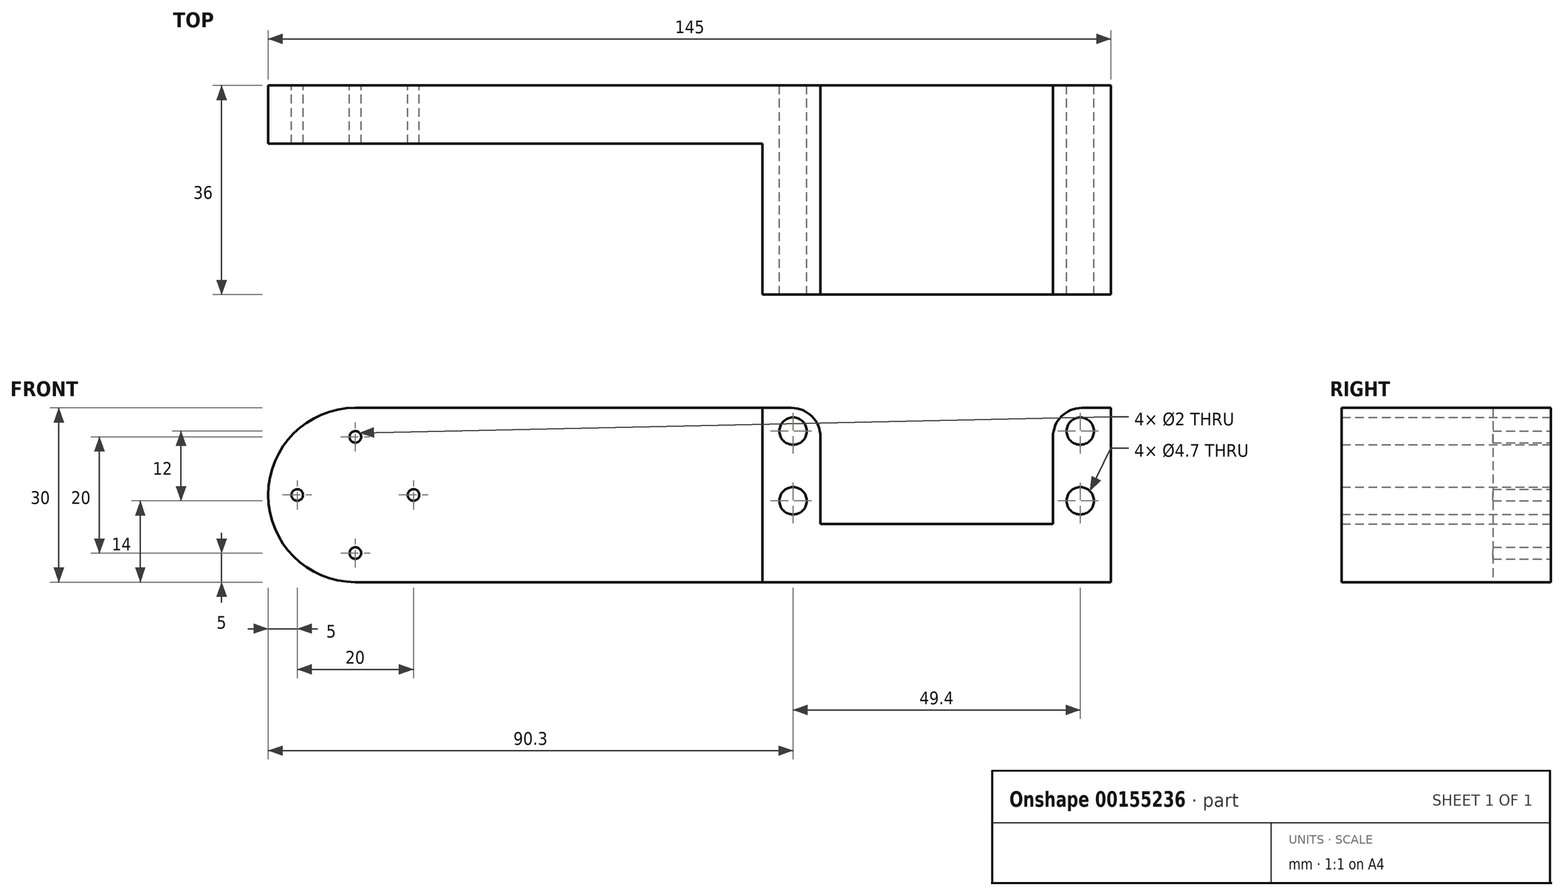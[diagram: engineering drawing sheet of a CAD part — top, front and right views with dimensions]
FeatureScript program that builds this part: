
annotation { "Feature Type Name" : "Feature", "Feature Type Description" : "" }
export const myFeature = defineFeature(function(context is Context, id is Id, definition is map)
    precondition{}
    {
        {
            var Q0;
            Q0=qCreatedBy(makeId("Front.planeOp"),FACE);
            var sketch = newSketch(context, id + "F0", { "sketchPlane" : qUnion([Q0])});
            skArc(sketch, "E0", {"start": v(-10, 5) * mm, "mid": v(-25, -10) * mm, "end": v(-10, -25) * mm});
            skLineSegment(sketch, "E1.bottom", {"start": v(-10, 5) * mm, "end": v(70, 5) * mm});
            skLineSegment(sketch, "E1.top", {"start": v(-10, -25) * mm, "end": v(120, -25) * mm});
            skLineSegment(sketch, "E1.right", {"start": v(120, 5) * mm, "end": v(120, -25) * mm});
            skCircle(sketch, "E2", {"center": v(-10, 0) * mm, "radius": 1 * mm});
            skCircle(sketch, "E3", {"center": v(-10, -20) * mm, "radius": 1 * mm});
            skCircle(sketch, "E4", {"center": v(-20, -10) * mm, "radius": 1 * mm});
            skCircle(sketch, "E5", {"center": v(0, -10) * mm, "radius": 1 * mm});
            skLineSegment(sketch, "E6.top", {"start": v(70, -15) * mm, "end": v(110, -15) * mm});
            skLineSegment(sketch, "E6.left", {"start": v(70, 5) * mm, "end": v(70, -15) * mm});
            skLineSegment(sketch, "E6.right", {"start": v(110, 5) * mm, "end": v(110, -15) * mm});
            skLineSegment(sketch, "E7.trimOffspring", {"start": v(110, 5) * mm, "end": v(120, 5) * mm});
            skCircle(sketch, "E8", {"center": v(114.7, -11) * mm, "radius": 2.35 * mm});
            skCircle(sketch, "E9", {"center": v(114.7, 1) * mm, "radius": 2.35 * mm});
            skCircle(sketch, "E10", {"center": v(65.3, 1) * mm, "radius": 2.35 * mm});
            skCircle(sketch, "E11", {"center": v(65.3, -11) * mm, "radius": 2.35 * mm});
            skSolve(sketch);
        }
        {
            var Q0;
            Q0 = qSketchRegion(id + "F0", true);
            extrude(context, id + "F1", {"entities" : qUnion([Q0]), "depth" : 36 * mm});
        }
        {
            var Q0;
            Q0=makeQuery(id+"F1.opExtrude","CAP_FACE",FACE,{"disambiguationData":[OSD([sQuery(id+"F0.wireOp",EDGE,"E0"),sQuery(id+"F0.wireOp",EDGE,"E1.bottom"),sQuery(id+"F0.wireOp",EDGE,"E1.top"),sQuery(id+"F0.wireOp",EDGE,"E1.right"),sQuery(id+"F0.wireOp",EDGE,"E2"),sQuery(id+"F0.wireOp",EDGE,"E3"),sQuery(id+"F0.wireOp",EDGE,"E4"),sQuery(id+"F0.wireOp",EDGE,"E5"),sQuery(id+"F0.wireOp",EDGE,"E6.top"),sQuery(id+"F0.wireOp",EDGE,"E6.left"),sQuery(id+"F0.wireOp",EDGE,"E6.right"),sQuery(id+"F0.wireOp",EDGE,"E7.trimOffspring"),sQuery(id+"F0.wireOp",EDGE,"E8"),sQuery(id+"F0.wireOp",EDGE,"E9"),sQuery(id+"F0.wireOp",EDGE,"E10"),sQuery(id+"F0.wireOp",EDGE,"E11")])],"isStart":false});
            var sketch = newSketch(context, id + "F2", { "sketchPlane" : qUnion([Q0])});
            skLineSegment(sketch, "E12.bottom", {"start": v(60, 5) * mm, "end": v(-215.68, 5) * mm});
            skLineSegment(sketch, "E12.top", {"start": v(60, -25) * mm, "end": v(-215.68, -25) * mm});
            skLineSegment(sketch, "E12.left", {"start": v(60, 5) * mm, "end": v(60, -25) * mm});
            skLineSegment(sketch, "E12.right", {"start": v(-215.68, 5) * mm, "end": v(-215.68, -25) * mm});
            skSolve(sketch);
        }
        {
            var Q0;
            Q0 = qSketchRegion(id + "F2", true);
            extrude(context, id + "F3", {"entities" : qUnion([Q0]), "operationType" : NewBodyOperationType.REMOVE, "oppositeDirection" : true, "depth" : 26 * mm});
        }
        {
            var Q0;
            Q0=makeQuery(id+"F1.opExtrude","SWEPT_EDGE",EDGE,{"disambiguationData":[OSD([sQuery(id+"F0.wireOp",EDGE,"E6.right"),sQuery(id+"F0.wireOp",EDGE,"E7.trimOffspring")])]});
            var Q1;
            Q1=makeQuery(id+"F1.opExtrude","SWEPT_EDGE",EDGE,{"disambiguationData":[OSD([sQuery(id+"F0.wireOp",EDGE,"E1.bottom"),sQuery(id+"F0.wireOp",EDGE,"E6.left")])]});
            fillet(context, id + "F4", {"entities" : qUnion([Q0, Q1]), "radius" : 5 * mm, "tangentPropagation" : true, "allowEdgeOverflow" : false});
        }
    });
